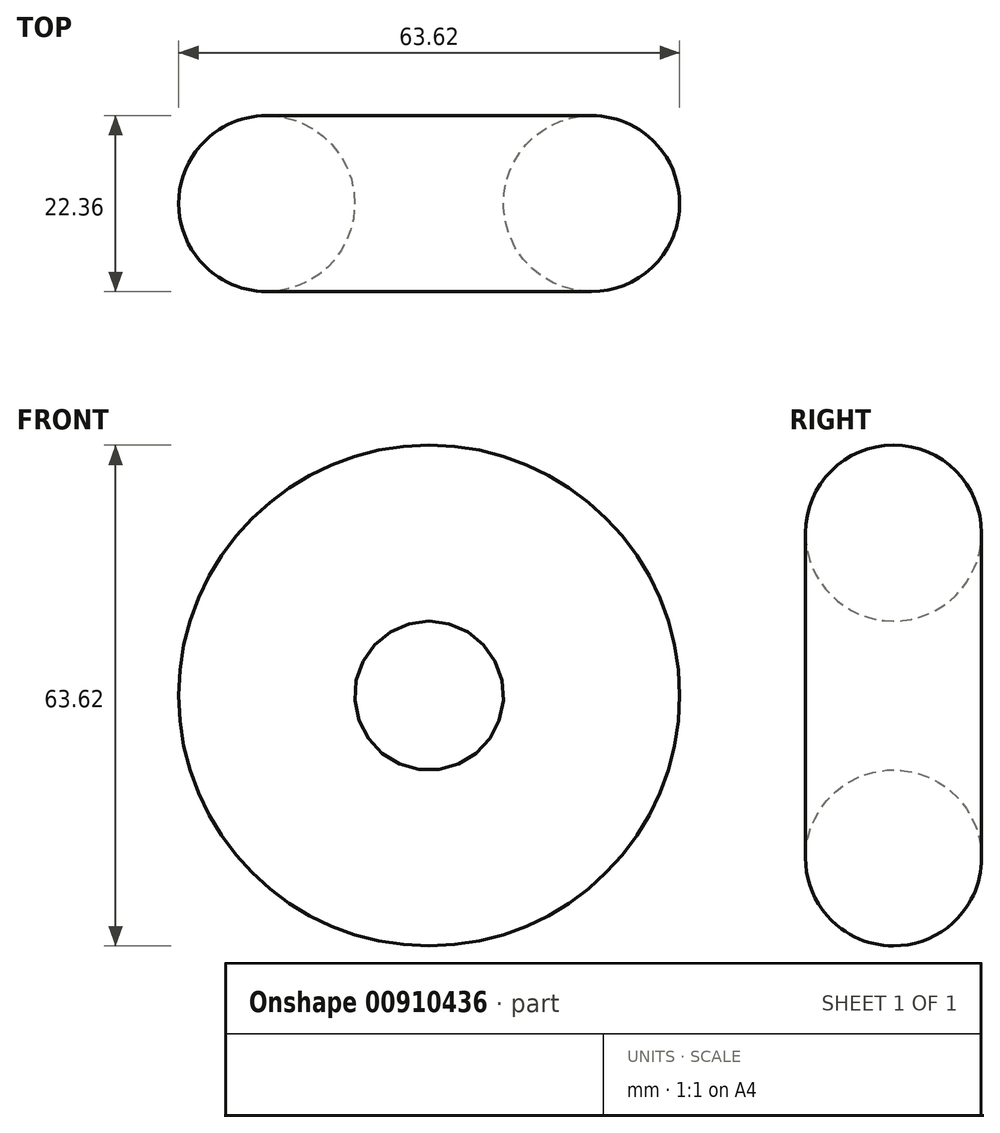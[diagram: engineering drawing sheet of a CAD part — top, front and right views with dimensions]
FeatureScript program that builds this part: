
annotation { "Feature Type Name" : "Feature", "Feature Type Description" : "" }
export const myFeature = defineFeature(function(context is Context, id is Id, definition is map)
    precondition{}
    {
        {
            var Q0;
            Q0=qCreatedBy(makeId("Top.planeOp"),FACE);
            var sketch = newSketch(context, id + "F0", { "sketchPlane" : qUnion([Q0])});
            skCircle(sketch, "E0", {"center": v(-62.28, 52.52) * mm, "radius": 11.18 * mm});
            skLineSegment(sketch, "E1.bottom", {"start": v(23.25, 37.16) * mm, "end": v(59.79, 37.16) * mm});
            skLineSegment(sketch, "E1.top", {"start": v(23.25, 15.57) * mm, "end": v(59.79, 15.57) * mm});
            skLineSegment(sketch, "E1.left", {"start": v(23.25, 37.16) * mm, "end": v(23.25, 15.57) * mm});
            skLineSegment(sketch, "E1.right", {"start": v(59.79, 37.16) * mm, "end": v(59.79, 15.57) * mm});
            skLineSegment(sketch, "E2", {"start": v(-55, -17.45) * mm, "end": v(-20.95, -29.08) * mm});
            skLineSegment(sketch, "E3", {"start": v(-20.95, -29.08) * mm, "end": v(-20.95, -63.13) * mm});
            skLineSegment(sketch, "E4", {"start": v(-20.95, -63.13) * mm, "end": v(-59.98, -69.35) * mm});
            skLineSegment(sketch, "E5", {"start": v(-59.98, -69.35) * mm, "end": v(-55, -17.45) * mm});
            skLineSegment(sketch, "E6", {"start": v(-82.91, 71.7) * mm, "end": v(-82.91, 30.26) * mm, "construction": true});
            skSolve(sketch);
        }
        {
            var Q0;
            Q0=qCreatedBy(makeId("Top.planeOp"),FACE);
            cPlane(context, id + "F1", {"entities" : qUnion([Q0]), "cplaneType" : CPlaneType.OFFSET, "offset" : 50.8 * mm, "width" : 152.4 * mm, "height" : 152.4 * mm});
        }
        {
            var Q0;
            Q0=makeQuery(id+"F0.imprint","IMPRINT",FACE,{"disambiguationData":[TD([[makeQuery(id+"F0.imprint","IMPRINT",EDGE,{"derivedFrom":sQuery(id+"F0.wireOp",EDGE,"E0")}),1.0]])]});
            var Q1;
            Q1=sQuery(id+"F0.wireOp",EDGE,"E6");
            revolve(context, id + "F2", {"surfaceOperationType" : NewSurfaceOperationType.NEW, "entities" : qUnion([Q0]), "axis" : qUnion([Q1]), "revolveType" : RevolveType.FULL});
        }
        {
            var Q0;
            Q0=sQuery(id+"F0.wireOp",EDGE,"E2");
            var Q1;
            Q1=sQuery(id+"F0.wireOp",EDGE,"E1.bottom");
            revolve(context, id + "F3", {"bodyType" : ToolBodyType.SURFACE, "surfaceOperationType" : NewSurfaceOperationType.NEW, "surfaceEntities" : qUnion([Q0]), "axis" : qUnion([Q1]), "revolveType" : RevolveType.FULL});
        }
    });
